# Revit family: Shower-Valve_Trim-KOHLER-Refinia-K-TS5320
name_source: partatom
category: Plumbing Fixtures
revit_build: Autodesk Revit 2015 (Build: 20140606_1530(x64)
units: mm (PartAtom-declared; Revit-internal decimal feet)

## types (4) — shared parameters
ADA Compliant = No
Assembly Code = D2010700
CW Connection = No
Cold Water Inlet = Cold Water Inlet
Date Modified = 09/07/2018
Default Elevation = 42"
Drain Included = No
HW Connection = Yes
Height = 6 7/16"
Hot Water Inlet = Tempered Water Inlet
Length = 7 5/16"
Manufacturer = KOHLER Co.
MasterFormat 1995 = 15410
MasterFormat 2004 = 22.41.23
Material = Premium Metal Finish
Pressure = 80.00 psi
Product Documentation Link = https://www.us.kohler.com
Product Name = Refinia
Product Page URL = https://www.us.kohler.com
URL = https://www.us.kohler.com
Vent Connection = No
Waste Connection = No
Waste Water Outlet = Waste Water Outlet
Width = 6 7/16"

## per-type parameters (varying)
| type | Description | Finish | Flow Rate | Model | Type |
| 2.5 GPM, CP-Polished Chrome | Rite-Temp shower valve trim with lever handle and 2.5 gpm showerhead | Kohler-Metal-CP-Polished_Chrome | 3 GPM | K-TS5320-4-CP | 1 |
| 2.5 GPM, BN-Vibrant Brushed Nickel | Rite-Temp shower valve trim with lever handle and 2.5 gpm showerhead | Kohler-Metal-BN-Vibrant_Brushed_Nickel | 3 GPM | K-TS5320-4-BN | 2 |
| 2GPM, CP-Polished Chrome | Rite-Temp shower trim set, valve not included | Kohler-Metal-CP-Polished_Chrome | 2 GPM | K-TS5320-4E-CP | 3 |
| 2GPM, BN Vibrant Brushed Nickel | Rite-Temp shower trim set, valve not included | Kohler-Metal-BN-Vibrant_Brushed_Nickel | 2 GPM | K-TS5320-4E-BN | 4 |

## geometry (parser evidence)
native form markers: Sweep x8
no freeform markers — native parametric forms only
